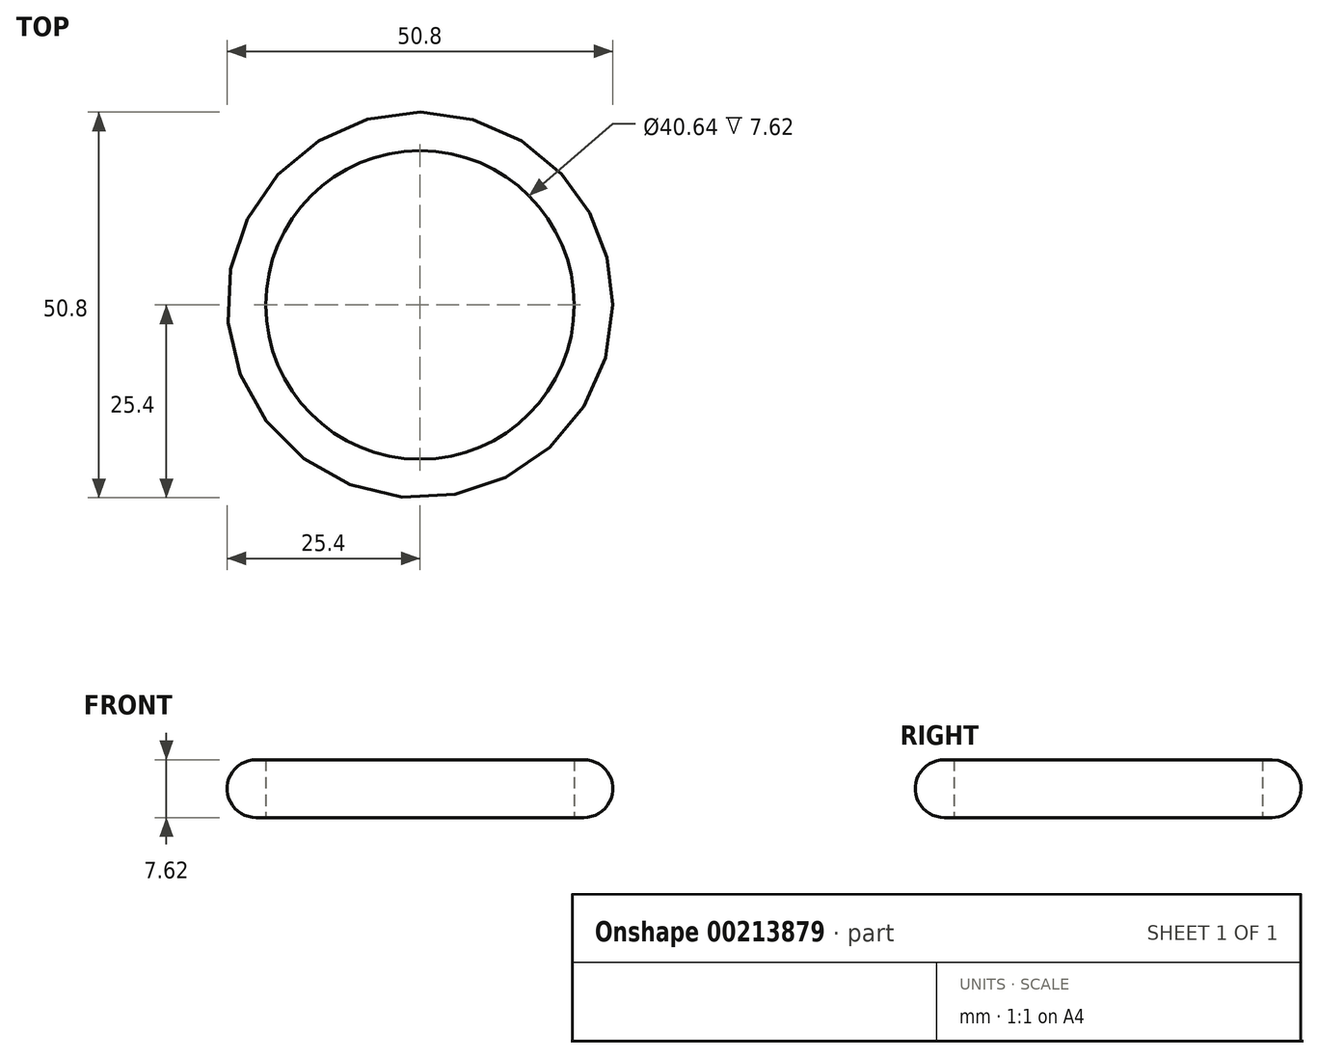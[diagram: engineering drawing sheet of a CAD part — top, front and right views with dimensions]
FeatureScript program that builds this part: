
annotation { "Feature Type Name" : "Feature", "Feature Type Description" : "" }
export const myFeature = defineFeature(function(context is Context, id is Id, definition is map)
    precondition{}
    {
        {
            var Q0;
            Q0=qCreatedBy(makeId("Top.planeOp"),FACE);
            var sketch = newSketch(context, id + "F1", { "sketchPlane" : qUnion([Q0])});
            skPoint(sketch, "E0", {"position": v(0, 0) * mm});
            skPoint(sketch, "E1", {"position": v(0, 20.32) * mm});
            skPoint(sketch, "E2", {"position": v(0, 25.4) * mm});
            skCircle(sketch, "E3", {"center": v(0, 0) * mm, "radius": 20.32 * mm});
            skCircle(sketch, "E4", {"center": v(0, 0) * mm, "radius": 25.4 * mm});
            skSolve(sketch);
        }
        {
            var Q0;
            Q0=makeQuery(id+"F1.imprint","IMPRINT",FACE,{"disambiguationData":[TD([[makeQuery(id+"F1.imprint","IMPRINT",EDGE,{"derivedFrom":sQuery(id+"F1.wireOp",EDGE,"E3")}),-1.0]])]});
            extrude(context, id + "F2", {"entities" : qUnion([Q0]), "depth" : 7.62 * mm});
        }
        {
            var Q0;
            Q0=makeQuery(id+"F2.opExtrude","CAP_EDGE",EDGE,{"disambiguationData":[OSD([sQuery(id+"F1.wireOp",EDGE,"E4")])],"isStart":true});
            fillet(context, id + "F3", {"entities" : qUnion([Q0]), "radius" : 3.8 * mm, "tangentPropagation" : true, "allowEdgeOverflow" : false});
        }
        {
            var Q0;
            Q0=makeQuery(id+"F2.opExtrude","CAP_EDGE",EDGE,{"disambiguationData":[OSD([sQuery(id+"F1.wireOp",EDGE,"E4")])],"isStart":false});
            fillet(context, id + "F0", {"entities" : qUnion([Q0]), "radius" : 3.8 * mm, "tangentPropagation" : true, "allowEdgeOverflow" : false});
        }
    });
